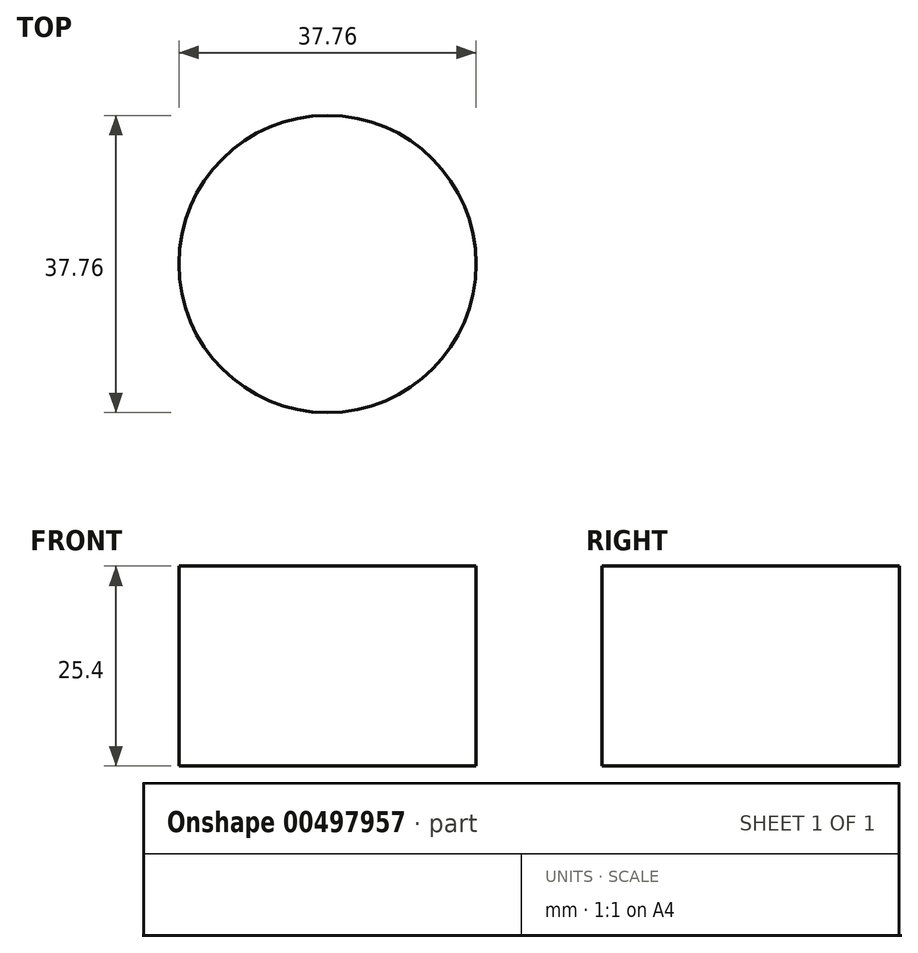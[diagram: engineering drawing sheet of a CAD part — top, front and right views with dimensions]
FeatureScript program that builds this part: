
annotation { "Feature Type Name" : "Feature", "Feature Type Description" : "" }
export const myFeature = defineFeature(function(context is Context, id is Id, definition is map)
    precondition{}
    {
        {
            var Q0;
            Q0=qCreatedBy(makeId("Top.planeOp"),FACE);
            var sketch = newSketch(context, id + "F0", { "sketchPlane" : qUnion([Q0])});
            skCircle(sketch, "E0", {"center": v(0, 0) * mm, "radius": 18.97 * mm});
            skSolve(sketch);
        }
        {
            var Q0;
            Q0=qCreatedBy(makeId("Top.planeOp"),FACE);
            var sketch = newSketch(context, id + "F1", { "sketchPlane" : qUnion([Q0])});
            skCircle(sketch, "E1", {"center": v(-66.77, 66.48) * mm, "radius": 18.88 * mm});
            skSolve(sketch);
        }
        {
            var Q0;
            Q0=qCreatedBy(makeId("Top.planeOp"),FACE);
            var sketch = newSketch(context, id + "F2", { "sketchPlane" : qUnion([Q0])});
            skCircle(sketch, "E2", {"center": v(0, -93.57) * mm, "radius": 18.97 * mm});
            skSolve(sketch);
        }
        {
            var Q0;
            Q0=qCreatedBy(makeId("Top.planeOp"),FACE);
            var sketch = newSketch(context, id + "F3", { "sketchPlane" : qUnion([Q0])});
            skCircle(sketch, "E3", {"center": v(76.75, 30.54) * mm, "radius": 18.97 * mm});
            skSolve(sketch);
        }
        {
            var Q0;
            Q0=qCreatedBy(makeId("Top.planeOp"),FACE);
            cPlane(context, id + "F4", {"entities" : qUnion([Q0]), "cplaneType" : CPlaneType.OFFSET, "offset" : 25.4 * mm, "width" : 152.4 * mm, "height" : 152.4 * mm});
        }
        {
            var Q0;
            Q0=qCreatedBy(id+"F4.planeOp",FACE);
            var sketch = newSketch(context, id + "F5", { "sketchPlane" : qUnion([Q0])});
            skCircle(sketch, "E4", {"center": v(-66.77, 66.48) * mm, "radius": 18.88 * mm});
            skCircle(sketch, "E5", {"center": v(0, 0) * mm, "radius": 18.97 * mm});
            skCircle(sketch, "E6", {"center": v(76.75, 30.54) * mm, "radius": 18.97 * mm});
            skCircle(sketch, "E7", {"center": v(0, -93.57) * mm, "radius": 18.97 * mm});
            skSolve(sketch);
        }
        {
            var Q0;
            Q0=makeQuery(id+"F5.imprint","IMPRINT",FACE,{"disambiguationData":[TD([[makeQuery(id+"F5.imprint","IMPRINT",EDGE,{"derivedFrom":sQuery(id+"F5.wireOp",EDGE,"E4")}),1.0]])]});
            var Q1;
            Q1=makeQuery(id+"F1.imprint","IMPRINT",FACE,{"disambiguationData":[TD([[makeQuery(id+"F1.imprint","IMPRINT",EDGE,{"derivedFrom":sQuery(id+"F1.wireOp",EDGE,"E1")}),1.0]])]});
            loft(context, id + "F6", {"sheetProfilesArray" : [{ "sheetProfileEntities" : qUnion([Q0]) }, { "sheetProfileEntities" : qUnion([Q1]) }]});
        }
    });
